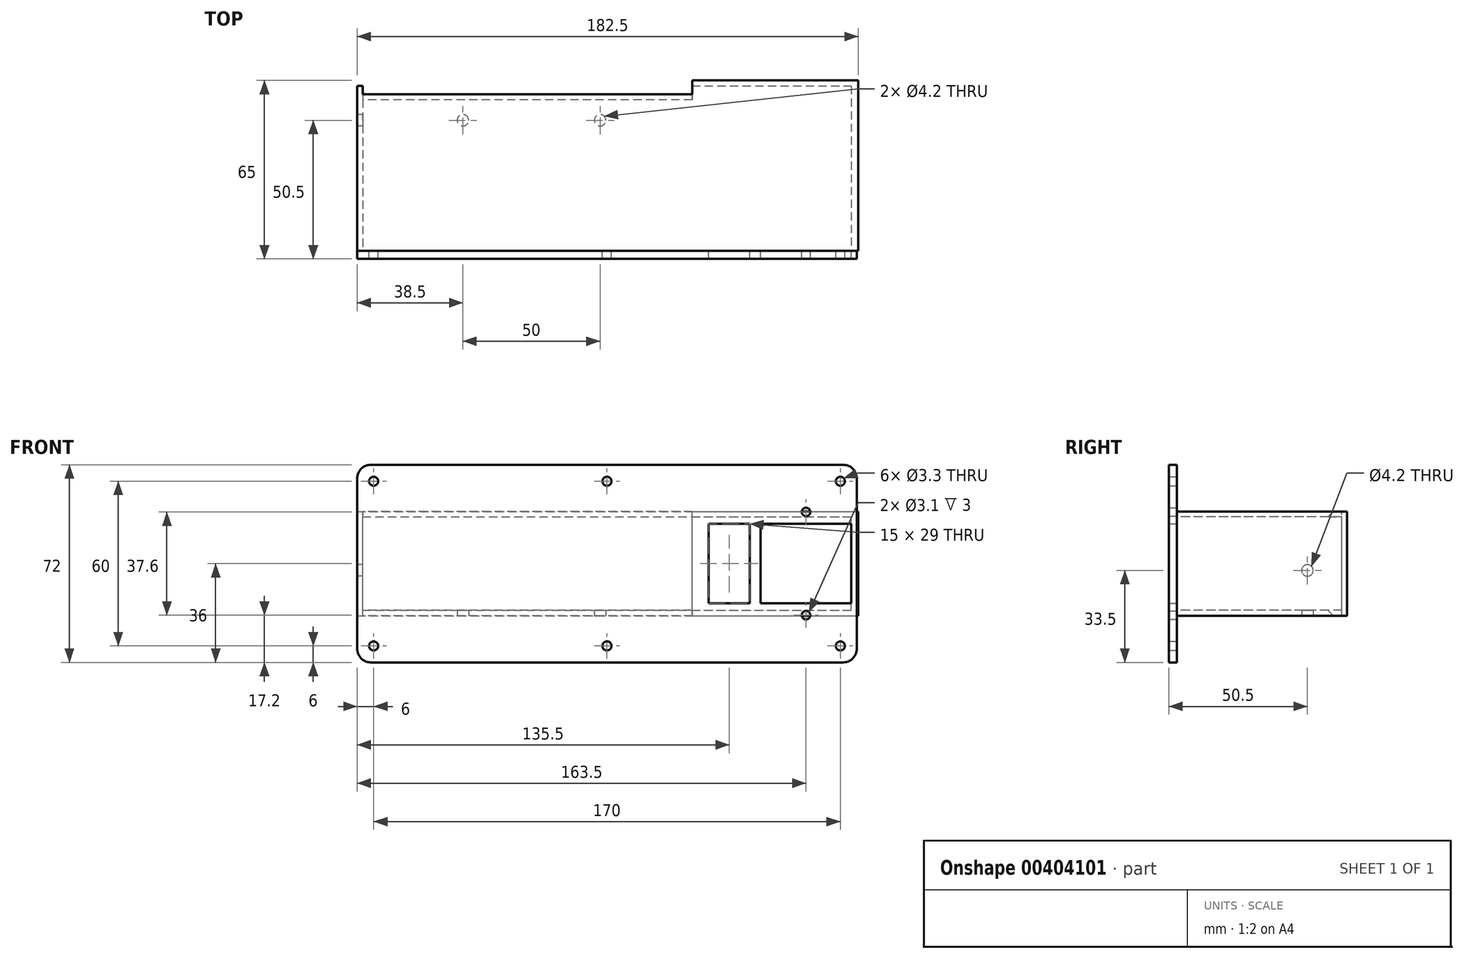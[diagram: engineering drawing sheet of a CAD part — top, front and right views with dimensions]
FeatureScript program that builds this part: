
annotation { "Feature Type Name" : "Feature", "Feature Type Description" : "" }
export const myFeature = defineFeature(function(context is Context, id is Id, definition is map)
    precondition{}
    {
        {
            var Q0;
            Q0=qCreatedBy(makeId("Front.planeOp"),FACE);
            var sketch = newSketch(context, id + "F0", { "sketchPlane" : qUnion([Q0])});
            skLineSegment(sketch, "E0.bottom", {"start": v(-86, 72) * mm, "end": v(86, 72) * mm});
            skLineSegment(sketch, "E0.top", {"start": v(-86, 0) * mm, "end": v(86, 0) * mm});
            skLineSegment(sketch, "E0.left", {"start": v(-91, 67) * mm, "end": v(-91, 5) * mm});
            skLineSegment(sketch, "E0.right", {"start": v(91, 67) * mm, "end": v(91, 5) * mm});
            skPoint(sketch, "E1", {"position": v(0, 0) * mm});
            skPoint(sketch, "E2.visualSharp", {"position": v(-91, 72) * mm});
            skArc(sketch, "E2.filletArc", {"start": v(-86, 72) * mm, "mid": v(-89.54, 70.54) * mm, "end": v(-91, 67) * mm});
            skPoint(sketch, "E3.visualSharp", {"position": v(91, 72) * mm});
            skArc(sketch, "E3.filletArc", {"start": v(91, 67) * mm, "mid": v(89.54, 70.54) * mm, "end": v(86, 72) * mm});
            skPoint(sketch, "E4.visualSharp", {"position": v(-91, 0) * mm});
            skArc(sketch, "E4.filletArc", {"start": v(-91, 5) * mm, "mid": v(-89.54, 1.46) * mm, "end": v(-86, 0) * mm});
            skPoint(sketch, "E5.visualSharp", {"position": v(91, 0) * mm});
            skArc(sketch, "E5.filletArc", {"start": v(86, 0) * mm, "mid": v(89.54, 1.46) * mm, "end": v(91, 5) * mm});
            skCircle(sketch, "E6", {"center": v(-85, 66) * mm, "radius": 1.65 * mm});
            skCircle(sketch, "E7", {"center": v(85, 66) * mm, "radius": 1.65 * mm});
            skCircle(sketch, "E8", {"center": v(-85, 6) * mm, "radius": 1.65 * mm});
            skCircle(sketch, "E9", {"center": v(85, 6) * mm, "radius": 1.65 * mm});
            skLineSegment(sketch, "E10.bottom", {"start": v(89, 50.5) * mm, "end": v(56, 50.5) * mm});
            skLineSegment(sketch, "E10.top", {"start": v(89, 21.5) * mm, "end": v(56, 21.5) * mm});
            skLineSegment(sketch, "E10.left", {"start": v(89, 50.5) * mm, "end": v(89, 21.5) * mm});
            skLineSegment(sketch, "E10.right", {"start": v(56, 50.5) * mm, "end": v(56, 21.5) * mm});
            skLineSegment(sketch, "E11.bottom", {"start": v(37, 50.5) * mm, "end": v(52, 50.5) * mm});
            skLineSegment(sketch, "E11.top", {"start": v(37, 21.5) * mm, "end": v(52, 21.5) * mm});
            skLineSegment(sketch, "E11.left", {"start": v(37, 50.5) * mm, "end": v(37, 21.5) * mm});
            skLineSegment(sketch, "E11.right", {"start": v(52, 50.5) * mm, "end": v(52, 21.5) * mm});
            skLineSegment(sketch, "E12.bottom", {"start": v(-85, 51) * mm, "end": v(30, 51) * mm, "construction": true});
            skLineSegment(sketch, "E12.top", {"start": v(-85, 21) * mm, "end": v(30, 21) * mm, "construction": true});
            skLineSegment(sketch, "E12.left", {"start": v(-85, 51) * mm, "end": v(-85, 21) * mm, "construction": true});
            skLineSegment(sketch, "E12.right", {"start": v(30, 51) * mm, "end": v(30, 21) * mm, "construction": true});
            skLineSegment(sketch, "E13", {"start": v(-91, 17) * mm, "end": v(91, 17) * mm, "construction": true});
            skLineSegment(sketch, "E14", {"start": v(91, 55) * mm, "end": v(-91, 55) * mm, "construction": true});
            skCircle(sketch, "E15", {"center": v(72.5, 17.2) * mm, "radius": 1.55 * mm});
            skCircle(sketch, "E16", {"center": v(72.5, 54.8) * mm, "radius": 1.55 * mm});
            skCircle(sketch, "E17", {"center": v(0, 66) * mm, "radius": 1.65 * mm});
            skCircle(sketch, "E18", {"center": v(0, 6) * mm, "radius": 1.65 * mm});
            skPoint(sketch, "E19", {"position": v(-91, 36) * mm});
            skPoint(sketch, "E20", {"position": v(-85, 36) * mm});
            skPoint(sketch, "E21", {"position": v(37, 36) * mm});
            skPoint(sketch, "E22", {"position": v(72.5, 50.5) * mm});
            skLineSegment(sketch, "E23", {"start": v(72.5, 50.5) * mm, "end": v(72.5, 55) * mm, "construction": true});
            skLineSegment(sketch, "E24", {"start": v(72.5, 21.5) * mm, "end": v(72.5, 17) * mm, "construction": true});
            skSolve(sketch);
        }
        {
            var Q0;
            Q0=makeQuery(id+"F0.imprint","IMPRINT",FACE,{"disambiguationData":[TD([[makeQuery(id+"F0.imprint","IMPRINT",EDGE,{"derivedFrom":sQuery(id+"F0.wireOp",EDGE,"E0.bottom")}),-1.0]])]});
            extrude(context, id + "F1", {"entities" : qUnion([Q0]), "depth" : 3 * mm});
        }
        {
            var Q0;
            Q0=makeQuery(id+"F0.imprint","IMPRINT",FACE,{"disambiguationData":[TD([[makeQuery(id+"F0.imprint","IMPRINT",EDGE,{"derivedFrom":sQuery(id+"F0.wireOp",EDGE,"E0.bottom")}),-1.0]])]});
            var sketch = newSketch(context, id + "F2", { "sketchPlane" : qUnion([Q0])});
            skLineSegment(sketch, "E25.bottom", {"start": v(-91, 17) * mm, "end": v(91.5, 17) * mm});
            skLineSegment(sketch, "E25.top", {"start": v(-91, 55) * mm, "end": v(91.5, 55) * mm});
            skLineSegment(sketch, "E25.left", {"start": v(-91, 17) * mm, "end": v(-91, 55) * mm});
            skLineSegment(sketch, "E25.right", {"start": v(91.5, 17) * mm, "end": v(91.5, 55) * mm});
            skLineSegment(sketch, "E26.bottom", {"start": v(-89, 19) * mm, "end": v(89, 19) * mm});
            skLineSegment(sketch, "E26.top", {"start": v(-89, 53) * mm, "end": v(89, 53) * mm});
            skLineSegment(sketch, "E26.left", {"start": v(-89, 19) * mm, "end": v(-89, 53) * mm});
            skLineSegment(sketch, "E26.right", {"start": v(89, 19) * mm, "end": v(89, 53) * mm});
            skSolve(sketch);
        }
        {
            var Q0;
            Q0=qSketchRegion(id+"F2",true);
            extrude(context, id + "F3", {"entities" : qUnion([Q0]), "operationType" : NewBodyOperationType.ADD, "oppositeDirection" : true, "depth" : 60 * mm});
        }
        {
            var Q0;
            Q0=makeQuery(id+"F3.opExtrude","SWEPT_FACE",FACE,{"disambiguationData":[OSD([sQuery(id+"F2.wireOp",EDGE,"E25.bottom")])]});
            var sketch = newSketch(context, id + "F4", { "sketchPlane" : qUnion([Q0])});
            skCircle(sketch, "E27", {"center": v(-52.5, -47.5) * mm, "radius": 2.1 * mm});
            skCircle(sketch, "E28", {"center": v(-2.5, -47.5) * mm, "radius": 2.1 * mm});
            skLineSegment(sketch, "E29", {"start": v(30, 0) * mm, "end": v(-2.5, 0) * mm, "construction": true});
            skLineSegment(sketch, "E30", {"start": v(-2.5, 0) * mm, "end": v(-52.5, 0) * mm, "construction": true});
            skLineSegment(sketch, "E31", {"start": v(-52.5, 0) * mm, "end": v(-85, 0) * mm, "construction": true});
            skSolve(sketch);
        }
        {
            var Q0;
            Q0=qSketchRegion(id+"F4",true);
            extrude(context, id + "F5", {"entities" : qUnion([Q0]), "operationType" : NewBodyOperationType.REMOVE, "oppositeDirection" : true, "depth" : 25 * mm});
        }
        {
            var Q0;
            Q0=makeQuery(id+"F3.boolean.opBoolean","MERGE",FACE,{"derivedFrom":[makeQuery(id+"F1.opExtrude","SWEPT_FACE",FACE,{"disambiguationData":[OSD([sQuery(id+"F0.wireOp",EDGE,"E0.left")])]}),makeQuery(id+"F3.opExtrude","SWEPT_FACE",FACE,{"disambiguationData":[OSD([sQuery(id+"F2.wireOp",EDGE,"E25.left")])]})]});
            var sketch = newSketch(context, id + "F6", { "sketchPlane" : qUnion([Q0])});
            skCircle(sketch, "E32", {"center": v(-47.5, 33.5) * mm, "radius": 2.1 * mm});
            skSolve(sketch);
        }
        {
            var Q0;
            Q0=qSketchRegion(id+"F6",true);
            extrude(context, id + "F7", {"entities" : qUnion([Q0]), "operationType" : NewBodyOperationType.REMOVE, "oppositeDirection" : true, "depth" : 25 * mm});
        }
        {
            var Q0;
            Q0=makeQuery(id+"F3.opExtrude","CAP_FACE",FACE,{"disambiguationData":[OSD([sQuery(id+"F2.wireOp",EDGE,"E25.bottom"),sQuery(id+"F2.wireOp",EDGE,"E25.top"),sQuery(id+"F2.wireOp",EDGE,"E25.left"),sQuery(id+"F2.wireOp",EDGE,"E25.right"),sQuery(id+"F2.wireOp",EDGE,"E26.bottom"),sQuery(id+"F2.wireOp",EDGE,"E26.top"),sQuery(id+"F2.wireOp",EDGE,"E26.left"),sQuery(id+"F2.wireOp",EDGE,"E26.right")])],"isStart":false});
            var sketch = newSketch(context, id + "F8", { "sketchPlane" : qUnion([Q0])});
            skLineSegment(sketch, "E33.bottom", {"start": v(-91.5, 17) * mm, "end": v(-31, 17) * mm});
            skLineSegment(sketch, "E33.top", {"start": v(-91.5, 55) * mm, "end": v(-31, 55) * mm});
            skLineSegment(sketch, "E33.left", {"start": v(-91.5, 17) * mm, "end": v(-91.5, 55) * mm});
            skLineSegment(sketch, "E33.right", {"start": v(-31, 17) * mm, "end": v(-31, 55) * mm});
            skSolve(sketch);
        }
        {
            var Q0;
            Q0=qSketchRegion(id+"F8",true);
            extrude(context, id + "F9", {"entities" : qUnion([Q0]), "operationType" : NewBodyOperationType.ADD, "depth" : 2 * mm});
        }
        {
            var Q0;
            Q0=makeQuery(id+"F3.opExtrude","CAP_EDGE",EDGE,{"disambiguationData":[OSD([sQuery(id+"F2.wireOp",EDGE,"E26.right")])],"isStart":false});
            var Q1;
            {var subQ0=sQuery(id+"F2.wireOp",EDGE,"E26.top");Q1=makeQuery(id+"F9.boolean.opBoolean","SPLIT",EDGE,{"disambiguationData":[TD([makeQuery(id+"F1.opExtrude","SWEPT_FACE",FACE,{"disambiguationData":[OSD([sQuery(id+"F0.wireOp",EDGE,"E10.left")])]})])],"derivedFrom":makeQuery(id+"F3.opExtrude","CAP_EDGE",EDGE,{"disambiguationData":[OSD([subQ0])],"isStart":false})});}
            var Q2;
            {var subQ0=sQuery(id+"F2.wireOp",EDGE,"E26.bottom");Q2=makeQuery(id+"F9.boolean.opBoolean","SPLIT",EDGE,{"disambiguationData":[TD([makeQuery(id+"F1.opExtrude","SWEPT_FACE",FACE,{"disambiguationData":[OSD([sQuery(id+"F0.wireOp",EDGE,"E10.left")])]})])],"derivedFrom":makeQuery(id+"F3.opExtrude","CAP_EDGE",EDGE,{"disambiguationData":[OSD([subQ0])],"isStart":false})});}
            chamfer(context, id + "F10", {"entities" : qUnion([Q0, Q1, Q2]), "width" : 5 * mm, "tangentPropagation" : true});
        }
    });
